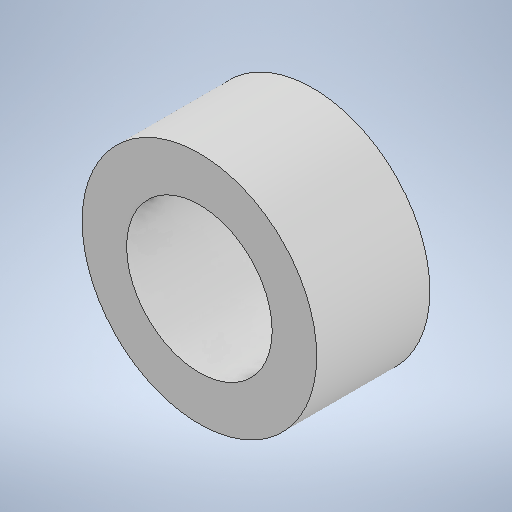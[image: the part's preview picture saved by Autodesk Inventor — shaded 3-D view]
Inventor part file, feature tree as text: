
AUTODESK INVENTOR PART (.ipt)
format: ipt  version: 2025.1 (Build 291241000, 241)  size: 218,112 bytes
history: native  units: mm
features: extrude x1, sketch x1
ambient origin geometry x8: Origin, YZ Plane, XZ Plane, XY Plane, X Axis, Y Axis, Z Axis, Center Point
bodies: Volumenkörper1 (feature_tree)
feature tree (2):
  extrude  "Extrusion1"  Depth=7.0mm
  sketch  "Skizze1"  dims[d0=14.5mm d1=9.0mm d2=7.0mm d3=0.0mm]
